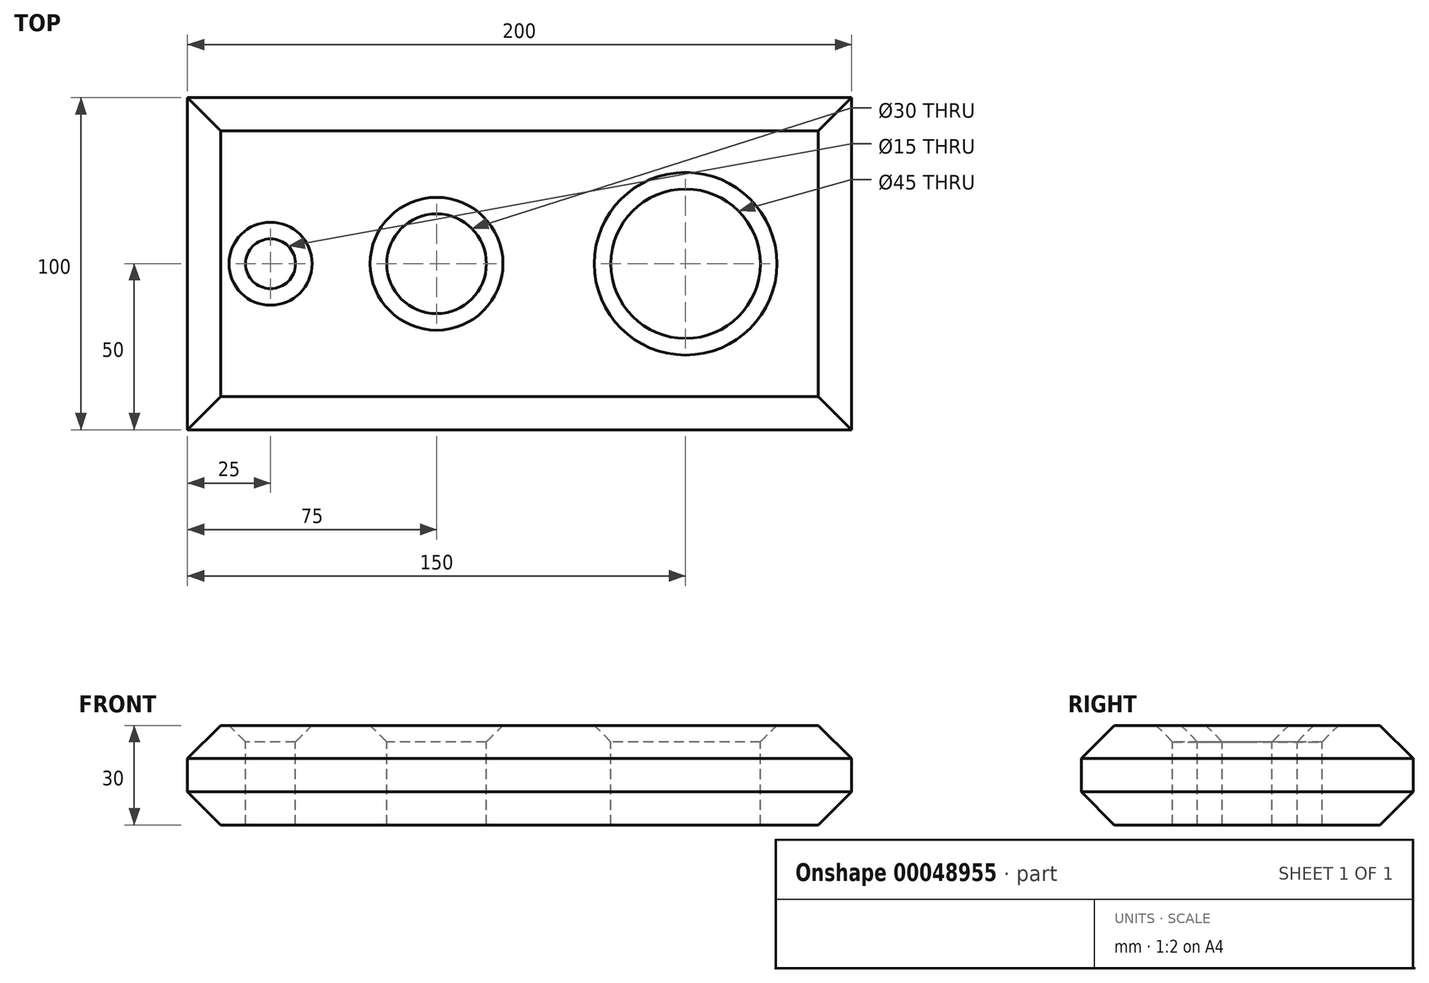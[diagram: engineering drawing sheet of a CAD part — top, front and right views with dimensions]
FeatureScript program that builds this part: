
annotation { "Feature Type Name" : "Feature", "Feature Type Description" : "" }
export const myFeature = defineFeature(function(context is Context, id is Id, definition is map)
    precondition{}
    {
        {
            var Q0;
            Q0=qCreatedBy(makeId("Top.planeOp"),FACE);
            var sketch = newSketch(context, id + "F0", { "sketchPlane" : qUnion([Q0])});
            skLineSegment(sketch, "E0.rect.bottom", {"start": v(100, 50) * mm, "end": v(-100, 50) * mm});
            skLineSegment(sketch, "E0.rect.top", {"start": v(100, -50) * mm, "end": v(-100, -50) * mm});
            skLineSegment(sketch, "E0.rect.left", {"start": v(100, 50) * mm, "end": v(100, -50) * mm});
            skLineSegment(sketch, "E0.rect.right", {"start": v(-100, 50) * mm, "end": v(-100, -50) * mm});
            skPoint(sketch, "E0.rect.middle", {"position": v(0, 0) * mm});
            skLineSegment(sketch, "E1", {"start": v(-100, 0) * mm, "end": v(-75, 0) * mm, "construction": true});
            skCircle(sketch, "E2", {"center": v(-75, 0) * mm, "radius": 7.5 * mm});
            skLineSegment(sketch, "E3", {"start": v(-75, 0) * mm, "end": v(-25, 0) * mm, "construction": true});
            skCircle(sketch, "E4", {"center": v(-25, 0) * mm, "radius": 15 * mm});
            skLineSegment(sketch, "E5", {"start": v(-25, 0) * mm, "end": v(50, 0) * mm, "construction": true});
            skCircle(sketch, "E6", {"center": v(50, 0) * mm, "radius": 22.5 * mm});
            skSolve(sketch);
        }
        {
            var Q0;
            Q0=qSketchRegion(id+"F0",true);
            extrude(context, id + "F1", {"entities" : qUnion([Q0]), "oppositeDirection" : true, "depth" : 30 * mm});
        }
        {
            var Q0;
            Q0=makeQuery(id+"F1.opExtrude","CAP_EDGE",EDGE,{"disambiguationData":[OSD([sQuery(id+"F0.wireOp",EDGE,"E2")])],"isStart":true});
            var Q1;
            Q1=makeQuery(id+"F1.opExtrude","CAP_EDGE",EDGE,{"disambiguationData":[OSD([sQuery(id+"F0.wireOp",EDGE,"E4")])],"isStart":true});
            var Q2;
            Q2=makeQuery(id+"F1.opExtrude","CAP_EDGE",EDGE,{"disambiguationData":[OSD([sQuery(id+"F0.wireOp",EDGE,"E6")])],"isStart":true});
            chamfer(context, id + "F2", {"entities" : qUnion([Q0, Q1, Q2]), "chamferType" : ChamferType.OFFSET_ANGLE, "width" : 5 * mm, "oppositeDirection" : false, "angle" : 45 * degree, "tangentPropagation" : true});
        }
        {
            var Q0;
            Q0=makeQuery(id+"F1.opExtrude","CAP_EDGE",EDGE,{"disambiguationData":[OSD([sQuery(id+"F0.wireOp",EDGE,"E0.rect.top")])],"isStart":true});
            var Q1;
            Q1=makeQuery(id+"F1.opExtrude","CAP_EDGE",EDGE,{"disambiguationData":[OSD([sQuery(id+"F0.wireOp",EDGE,"E0.rect.left")])],"isStart":true});
            var Q2;
            Q2=makeQuery(id+"F1.opExtrude","CAP_EDGE",EDGE,{"disambiguationData":[OSD([sQuery(id+"F0.wireOp",EDGE,"E0.rect.left")])],"isStart":false});
            var Q3;
            Q3=makeQuery(id+"F1.opExtrude","CAP_EDGE",EDGE,{"disambiguationData":[OSD([sQuery(id+"F0.wireOp",EDGE,"E0.rect.top")])],"isStart":false});
            var Q4;
            Q4=makeQuery(id+"F1.opExtrude","CAP_EDGE",EDGE,{"disambiguationData":[OSD([sQuery(id+"F0.wireOp",EDGE,"E0.rect.bottom")])],"isStart":true});
            var Q5;
            Q5=makeQuery(id+"F1.opExtrude","CAP_EDGE",EDGE,{"disambiguationData":[OSD([sQuery(id+"F0.wireOp",EDGE,"E0.rect.bottom")])],"isStart":false});
            var Q6;
            Q6=makeQuery(id+"F1.opExtrude","CAP_EDGE",EDGE,{"disambiguationData":[OSD([sQuery(id+"F0.wireOp",EDGE,"E0.rect.right")])],"isStart":false});
            var Q7;
            Q7=makeQuery(id+"F1.opExtrude","CAP_EDGE",EDGE,{"disambiguationData":[OSD([sQuery(id+"F0.wireOp",EDGE,"E0.rect.right")])],"isStart":true});
            chamfer(context, id + "F3", {"entities" : qUnion([Q0, Q1, Q2, Q3, Q4, Q5, Q6, Q7]), "chamferType" : ChamferType.OFFSET_ANGLE, "width" : 10 * mm, "oppositeDirection" : false, "angle" : 45 * degree, "tangentPropagation" : true});
        }
    });
